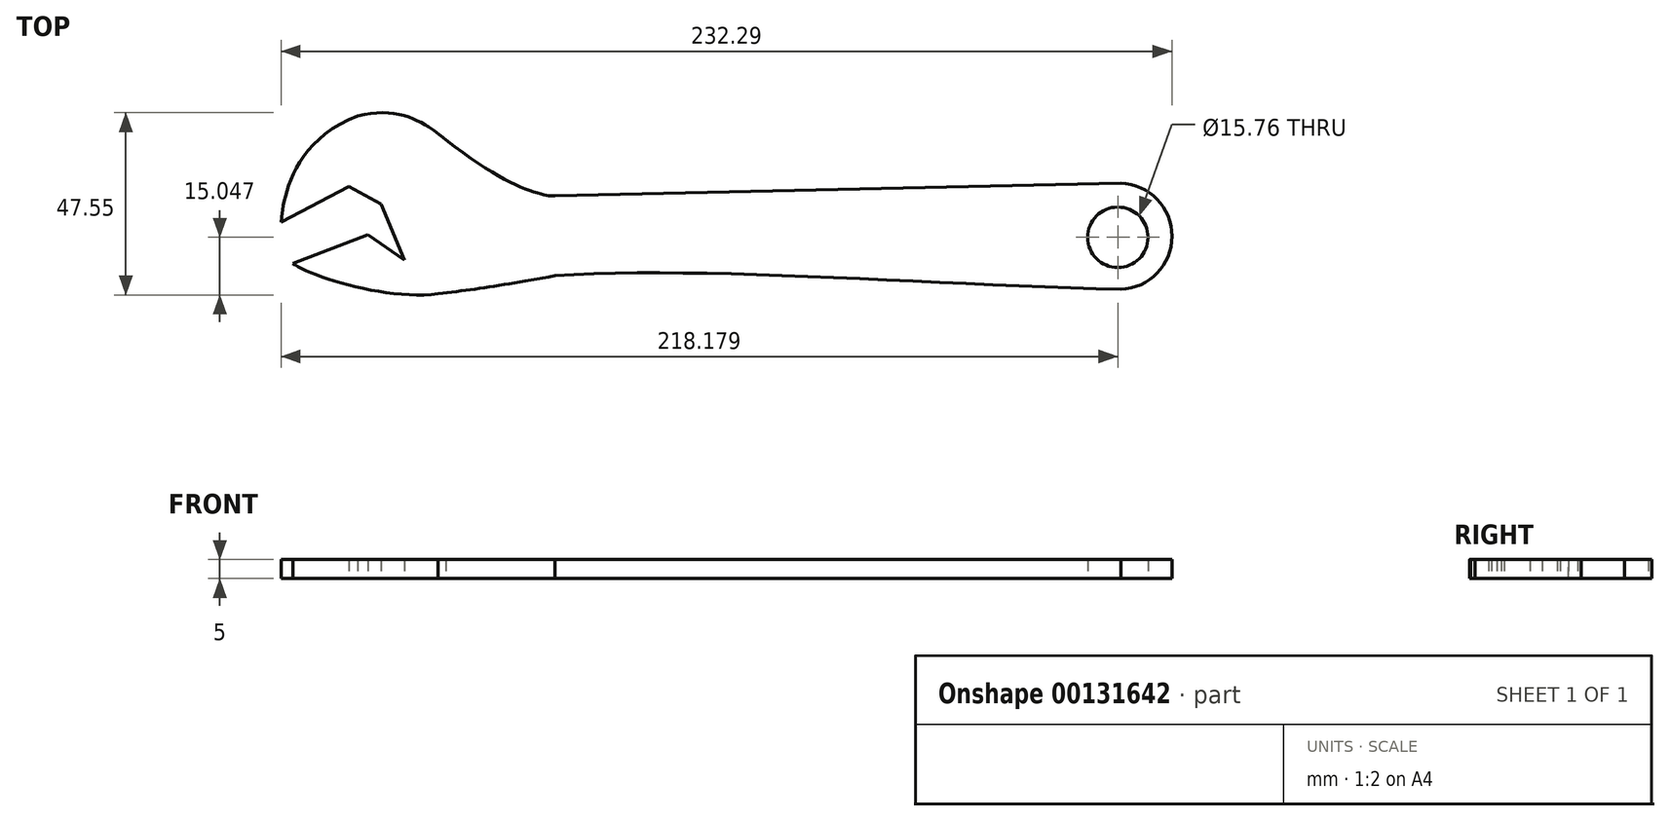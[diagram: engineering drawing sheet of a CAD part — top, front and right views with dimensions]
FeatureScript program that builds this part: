
annotation { "Feature Type Name" : "Feature", "Feature Type Description" : "" }
export const myFeature = defineFeature(function(context is Context, id is Id, definition is map)
    precondition{}
    {
        {
            var Q0;
            Q0=qCreatedBy(makeId("Top.planeOp"),FACE);
            var sketch = newSketch(context, id + "F0", { "sketchPlane" : qUnion([Q0])});
            skCircle(sketch, "E0", {"center": v(86.4, -19.26) * mm, "radius": 7.88 * mm});
            skPoint(sketch, "E0.first.point", {"position": v(86.08, -11.4) * mm});
            skPoint(sketch, "E0.second.point", {"position": v(86.8, -27.13) * mm});
            skPoint(sketch, "E0.third.point", {"position": v(94.1, -20.93) * mm});
            skLineSegment(sketch, "E1", {"start": v(-131.77, -15.34) * mm, "end": v(-114.1, -6.05) * mm});
            skLineSegment(sketch, "E2", {"start": v(-114.1, -6.05) * mm, "end": v(-105.68, -10.58) * mm});
            skLineSegment(sketch, "E3", {"start": v(-105.68, -10.58) * mm, "end": v(-99.6, -25.22) * mm});
            skLineSegment(sketch, "E4", {"start": v(-99.6, -25.22) * mm, "end": v(-109.07, -18.54) * mm});
            skLineSegment(sketch, "E5", {"start": v(-109.07, -18.54) * mm, "end": v(-128.63, -26.04) * mm});
            skFitSpline(sketch, "E6", {"points": [v(-128.63, -26.04) * mm, v(-90.85, -33.97) * mm], "startDerivative": vector(11.72, -9.75) * mm, "endDerivative": vector(40.16, 5.71) * mm});
            skFitSpline(sketch, "E7", {"points": [v(-131.77, -15.34) * mm, v(-111.8, 12.36) * mm], "startDerivative": vector(0.97, 5.08) * mm, "endDerivative": vector(58, 21.21) * mm});
            skFitSpline(sketch, "E8", {"points": [v(-111.8, 12.36) * mm, v(-88.8, 6.15) * mm], "startDerivative": vector(40.14, 11.12) * mm, "endDerivative": vector(3.67, -2.39) * mm});
            skFitSpline(sketch, "E9", {"points": [v(-88.8, 6.15) * mm, v(-60.38, -8.47) * mm], "startDerivative": vector(52.69, -41.35) * mm, "endDerivative": vector(5.6, 0.32) * mm});
            skLineSegment(sketch, "E10", {"start": v(-60.38, -8.47) * mm, "end": v(87.16, -5.11) * mm});
            skFitSpline(sketch, "E11", {"points": [v(-90.85, -33.97) * mm, v(-60.38, -29.27) * mm], "startDerivative": vector(27.89, 3.23) * mm, "endDerivative": vector(37.93, 7.18) * mm});
            skFitSpline(sketch, "E12", {"points": [v(-60.38, -29.27) * mm, v(87.16, -32.86) * mm], "startDerivative": vector(111.82, 7.96) * mm, "endDerivative": vector(147.53, -3.59) * mm});
            skArc(sketch, "E13", {"start": v(87.16, -32.86) * mm, "mid": v(100.52, -18.98) * mm, "end": v(87.16, -5.11) * mm});
            skSolve(sketch);
        }
        {
            var Q0;
            Q0=makeQuery(id+"F0.imprint","IMPRINT",FACE,{"disambiguationData":[TD([[makeQuery(id+"F0.imprint","IMPRINT",EDGE,{"derivedFrom":sQuery(id+"F0.wireOp",EDGE,"E0")}),-1.0]])]});
            extrude(context, id + "F1", {"entities" : qUnion([Q0]), "depth" : 5 * mm});
        }
    });
